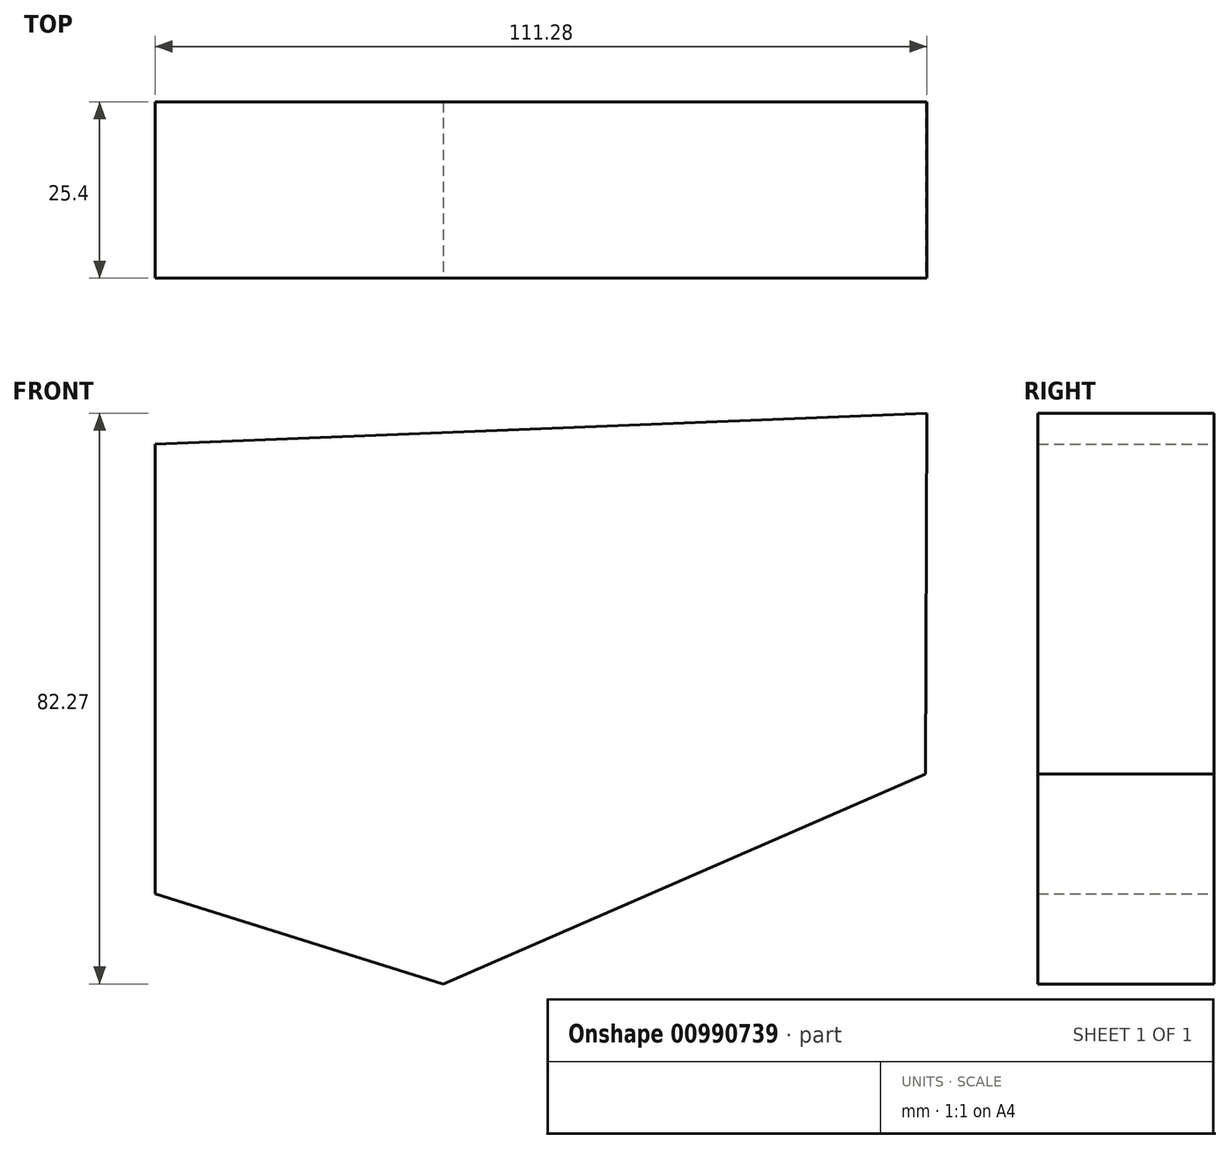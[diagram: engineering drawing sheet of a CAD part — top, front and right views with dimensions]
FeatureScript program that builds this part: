
annotation { "Feature Type Name" : "Feature", "Feature Type Description" : "" }
export const myFeature = defineFeature(function(context is Context, id is Id, definition is map)
    precondition{}
    {
        {
            var Q0;
            Q0=qCreatedBy(makeId("Front.planeOp"),FACE);
            var sketch = newSketch(context, id + "F0", { "sketchPlane" : qUnion([Q0])});
            skLineSegment(sketch, "E0", {"start": v(-62.32, 38) * mm, "end": v(-62.32, -26.84) * mm});
            skLineSegment(sketch, "E1", {"start": v(-62.32, -26.84) * mm, "end": v(48.49, -61.58) * mm});
            skLineSegment(sketch, "E2", {"start": v(48.49, -61.58) * mm, "end": v(48.96, 42.42) * mm});
            skLineSegment(sketch, "E3", {"start": v(48.96, 42.42) * mm, "end": v(-62.32, 38) * mm});
            skLineSegment(sketch, "E4", {"start": v(48.49, -61.58) * mm, "end": v(65.29, -53.52) * mm});
            skLineSegment(sketch, "E5", {"start": v(65.29, -53.52) * mm, "end": v(48.96, 42.42) * mm});
            skSolve(sketch);
        }
        {
            var Q0;
            Q0=makeQuery(id+"F0.imprint","IMPRINT",FACE,{"disambiguationData":[TD([[makeQuery(id+"F0.imprint","IMPRINT",EDGE,{"derivedFrom":sQuery(id+"F0.wireOp",EDGE,"E0")}),1.0]])]});
            extrude(context, id + "F1", {"entities" : qUnion([Q0]), "depth" : 25.4 * mm, "offsetDistance" : 25.4 * mm});
        }
        {
            var Q0;
            Q0=makeQuery(id+"F1.opExtrude","CAP_FACE",FACE,{"disambiguationData":[OSD([sQuery(id+"F0.wireOp",EDGE,"E0"),sQuery(id+"F0.wireOp",EDGE,"E1"),sQuery(id+"F0.wireOp",EDGE,"E2"),sQuery(id+"F0.wireOp",EDGE,"E3")])],"isStart":false});
            var sketch = newSketch(context, id + "F2", { "sketchPlane" : qUnion([Q0])});
            skLineSegment(sketch, "E6", {"start": v(48.72, -9.58) * mm, "end": v(-20.82, -39.85) * mm});
            skSolve(sketch);
        }
        {
            var Q0;
            {var subQ0=sQuery(id+"F2.wireOp",EDGE,"E6");Q0=makeQuery(id+"F2.imprint","IMPRINT",FACE,{"disambiguationData":[TD([[makeQuery(id+"F2.imprint","IMPRINT",EDGE,{"derivedFrom":subQ0}),1.0]])]});}
            extrude(context, id + "F3", {"entities" : qUnion([Q0]), "operationType" : NewBodyOperationType.REMOVE, "oppositeDirection" : true, "depth" : 25.4 * mm, "offsetDistance" : 25.4 * mm});
        }
    });
